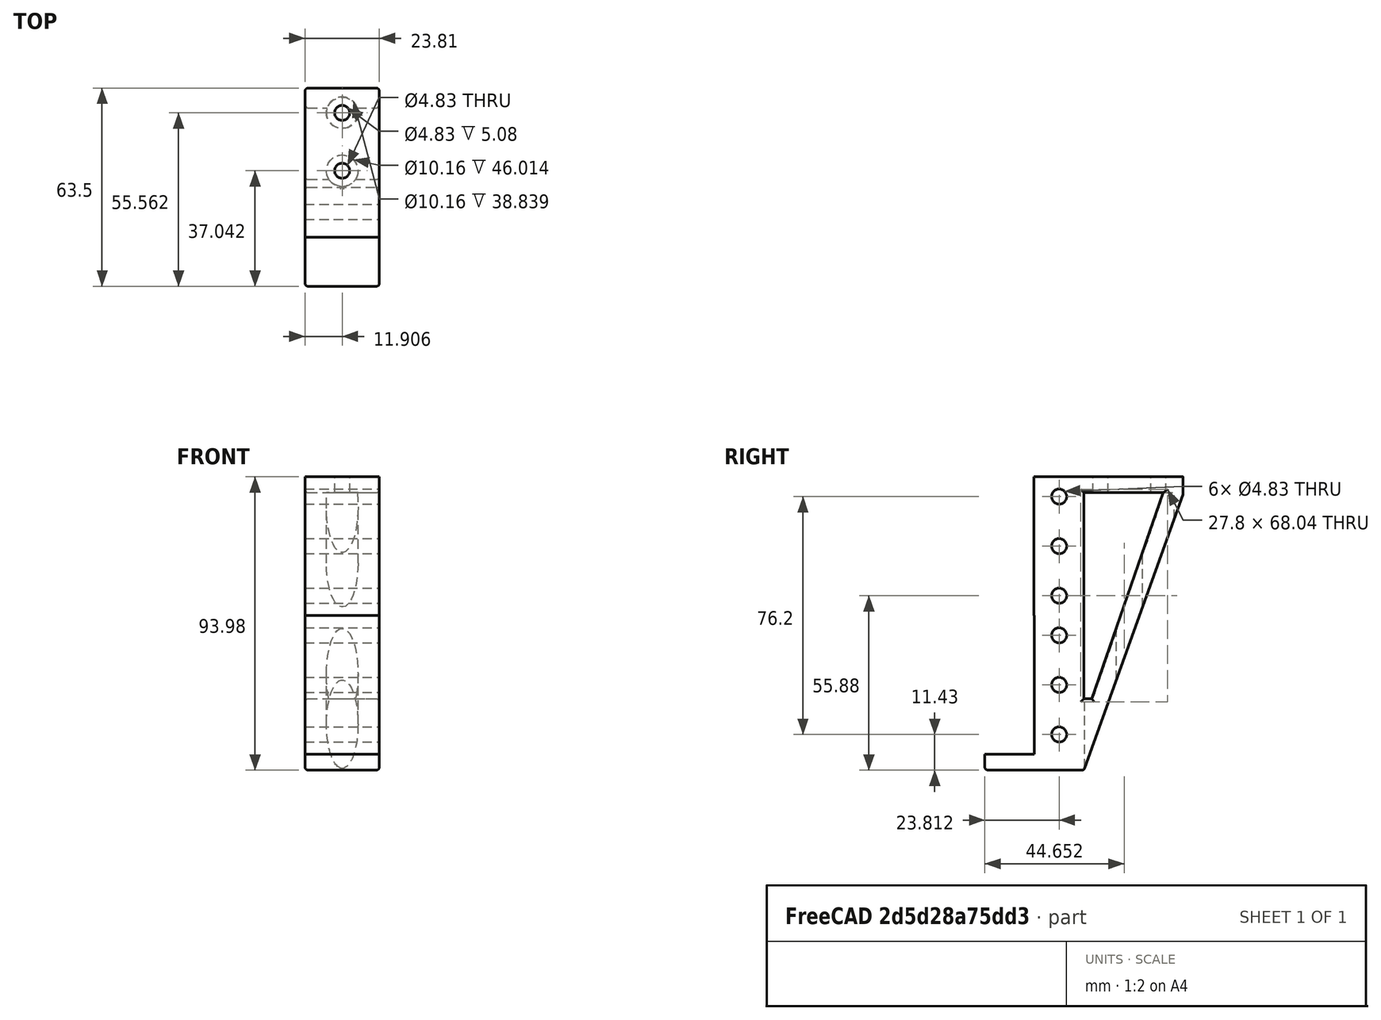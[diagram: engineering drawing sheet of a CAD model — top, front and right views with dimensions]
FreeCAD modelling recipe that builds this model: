
FCSTD DOCUMENT  (FreeCAD 0.18R15380 (Git))
Label: Rack_bracket
License: All rights reserved
LicenseURL: http://en.wikipedia.org/wiki/All_rights_reserved
objects: Part::Cut×12, Part::Cylinder×8, Part::Box×4, Part::MultiFuse×2, Spreadsheet::Sheet×1, Part::Wedge×1, Part::Fillet×1
note: 28 computed .brp shape members not serialized (recipe doc carries the construction recipe); baked Part::Feature solids carry a one-line shape summary decoded from their .brp

FEATURE [Part::Box] Box001  label="server"
  AttacherType = Attacher::AttachEngine3D
  Height = 44.45
  Length = 23.8125
  Placement = pos=(0,0,5.08) rot=(0,0,1;0rad)
  Width = 15.875
  expr: Placement.Base.z = Rack.U_separation * 2
  expr: Length = main_block.Length
FEATURE [Spreadsheet::Sheet] Spreadsheet  label="Rack"
  cells = A1(rail_width)==0.625"; A2(U_separation)==0.10000000000000001"; A3(U_height)==1.75"; A4(screw_hole)==0.19"
FEATURE [Part::Box] Box002  label="server001"
  AttacherType = Attacher::AttachEngine3D
  Height = 44.45
  Length = 23.8125
  Placement = pos=(0,0,49.53) rot=(0,0,1;0rad)
  Width = 15.748
  expr: Height = Rack.U_height
  expr: Placement.Base.z = Rack.U_separation * 2 + Rack.U_height
  expr: Length = main_block.Length
FEATURE [Part::Cylinder] Cylinder  label="ear_hole"
  Angle = 360
  AttacherType = Attacher::AttachEngine3D
  Height = 23.8125
  Placement = pos=(0,23.8125,11.43) rot=(0,1,0;1.5708rad)
  Radius = 2.413
  expr: Placement.Base.z = Rack.U_separation * 2 + 0.25"
  expr: Placement.Base.y = Rack.rail_width + Rack.rail_width / 2
  expr: Height = main_block.Length
  expr: Radius = Rack.screw_hole / 2
FEATURE [Part::Cylinder] Cylinder001
  Angle = 360
  AttacherType = Attacher::AttachEngine3D
  Height = 23.8125
  Placement = pos=(0,23.8125,27.305) rot=(0,1,0;1.5708rad)
  Radius = 2.413
  expr: Placement.Base.z = ear_hole.Placement.Base.z + 0.625"
  expr: Placement.Base.y = Rack.rail_width + Rack.rail_width / 2
  expr: Height = main_block.Length
  expr: Radius = Rack.screw_hole / 2
FEATURE [Part::Cylinder] Cylinder002
  Angle = 360
  AttacherType = Attacher::AttachEngine3D
  Height = 23.8125
  Placement = pos=(0,23.8125,43.18) rot=(0,1,0;1.5708rad)
  Radius = 2.413
  expr: Placement.Base.z = Cylinder001.Placement.Base.z + 0.625"
  expr: Placement.Base.y = Rack.rail_width + Rack.rail_width / 2
  expr: Height = main_block.Length
  expr: Radius = Rack.screw_hole / 2
FEATURE [Part::Cylinder] Cylinder003
  Angle = 360
  AttacherType = Attacher::AttachEngine3D
  Height = 23.8125
  Placement = pos=(0,23.8125,55.88) rot=(0,1,0;1.5708rad)
  Radius = 2.413
  expr: Placement.Base.z = Cylinder002.Placement.Base.z + 0.5"
  expr: Placement.Base.y = Rack.rail_width + Rack.rail_width / 2
  expr: Height = main_block.Length
  expr: Radius = Rack.screw_hole / 2
FEATURE [Part::Cylinder] Cylinder004
  Angle = 360
  AttacherType = Attacher::AttachEngine3D
  Height = 23.8125
  Placement = pos=(0,23.8125,71.755) rot=(0,1,0;1.5708rad)
  Radius = 2.413
  expr: Placement.Base.z = Cylinder003.Placement.Base.z + 0.625"
  expr: Placement.Base.y = Rack.rail_width + Rack.rail_width / 2
  expr: Height = main_block.Length
  expr: Radius = Rack.screw_hole / 2
FEATURE [Part::Cylinder] Cylinder005
  Angle = 360
  AttacherType = Attacher::AttachEngine3D
  Height = 23.8125
  Placement = pos=(0,23.8125,87.63) rot=(0,1,0;1.5708rad)
  Radius = 2.413
  expr: Placement.Base.z = Cylinder004.Placement.Base.z + 0.625"
  expr: Placement.Base.y = Rack.rail_width + Rack.rail_width / 2
  expr: Height = main_block.Length
  expr: Radius = Rack.screw_hole / 2
FEATURE [Part::Box] Box003  label="Cube"
  AttacherType = Attacher::AttachEngine3D
  Height = 109.25
  Length = 23.8125
  Placement = pos=(0,31.75,0) rot=(-1,0,0;0.344619rad)
  Width = 127
  expr: Placement.Rotation.Angle = asin((main_block.Width - Rack.rail_width * 2) / main_block.Height)
  expr: Height = sqrt(pow(main_block.Height - Rack.U_separation * 2; 2) + pow(main_block.Width; 2))
  expr: Placement.Base.y = Rack.rail_width * 2
  expr: Length = main_block.Length
FEATURE [Part::Cylinder] Cylinder006
  Angle = 360
  AttacherType = Attacher::AttachEngine3D
  Height = 93.98
  Radius = 2.413
  expr: Radius = Rack.screw_hole / 2
  expr: Height = main_block.Height
FEATURE [Part::Cylinder] Cylinder007
  Angle = 360
  AttacherType = Attacher::AttachEngine3D
  Height = 88.9
  Radius = 5.08
  expr: Height = main_block.Height - Rack.U_separation * 2
FEATURE [Part::MultiFuse] Fusion  label="TopMountHoleClose"
  Placement = pos=(11.9062,37.0417,0) rot=(0,0,1;0rad)
  Shapes = -> [Cylinder006,Cylinder007]
  expr: Placement.Base.y = Rack.rail_width * 2 + (main_block.Width - Rack.rail_width * 2) / 6
  expr: Placement.Base.x = main_block.Length * 1 / 2
FEATURE [Part::MultiFuse] Fusion002  label="TopMountHoleFar"
  Placement = pos=(11.9062,55.5625,0) rot=(0,0,1;0rad)
  Shapes = -> [Cylinder006,Cylinder007]
  expr: Placement.Base.y = Rack.rail_width * 2 + (main_block.Width - Rack.rail_width * 2) * 3 / 4
  expr: Placement.Base.x = main_block.Length * 1 / 2
FEATURE [Part::Wedge] Wedge
  AttacherType = Attacher::AttachEngine3D
  Placement = pos=(0,31.75,88.9) rot=(-1,0,0;1.5708rad)
  X2max = 23.8125
  X2min = 0
  Xmax = 23.8125
  Xmin = 0
  Ymax = 66.04
  Ymin = 0
  Z2max = 2.54
  Z2min = 0
  Zmax = 25.4
  Zmin = 0
  expr: Placement.Base.y = Rack.rail_width * 2
  expr: X2max = main_block.Length
  expr: Xmax = main_block.Length
FEATURE [Part::Box] Box  label="main_block"
  AttacherType = Attacher::AttachEngine3D
  Height = 93.98
  Length = 23.8125
  Width = 63.5
  expr: Length = 0.625in * 1.5
  expr: Height = Rack.U_height * 2 + Rack.U_separation * 2
FEATURE [Part::Cut] Cut
  Base = -> Box
  Tool = -> Box001
FEATURE [Part::Cut] Cut001
  Base = -> Cut
  Tool = -> Box002
FEATURE [Part::Cut] Cut002
  Base = -> Cut001
  Tool = -> Cylinder
FEATURE [Part::Cut] Cut003
  Base = -> Cut002
  Tool = -> Cylinder001
FEATURE [Part::Cut] Cut004
  Base = -> Cut003
  Tool = -> Cylinder002
FEATURE [Part::Cut] Cut005
  Base = -> Cut004
  Tool = -> Cylinder003
FEATURE [Part::Cut] Cut006
  Base = -> Cut005
  Tool = -> Cylinder004
FEATURE [Part::Cut] Cut007
  Base = -> Cut006
  Tool = -> Cylinder005
FEATURE [Part::Cut] Cut008
  Base = -> Cut007
  Tool = -> Box003
FEATURE [Part::Cut] Cut009
  Base = -> Cut008
  Tool = -> Fusion
FEATURE [Part::Cut] Cut011
  Base = -> Cut009
  Tool = -> Fusion002
FEATURE [Part::Cut] Cut013
  Base = -> Cut011
  Tool = -> Wedge
FEATURE [Part::Fillet] Fillet
  Base = -> Cut013
  Edges = 19 edges r=1: [Edge1,Edge2,Edge4,Edge6,Edge15,Edge16,Edge17,Edge18,Edge20,Edge22,Edge23,Edge24,Edge27,Edge28,Edge33,Edge52,Edge60,Edge61,Edge67]
